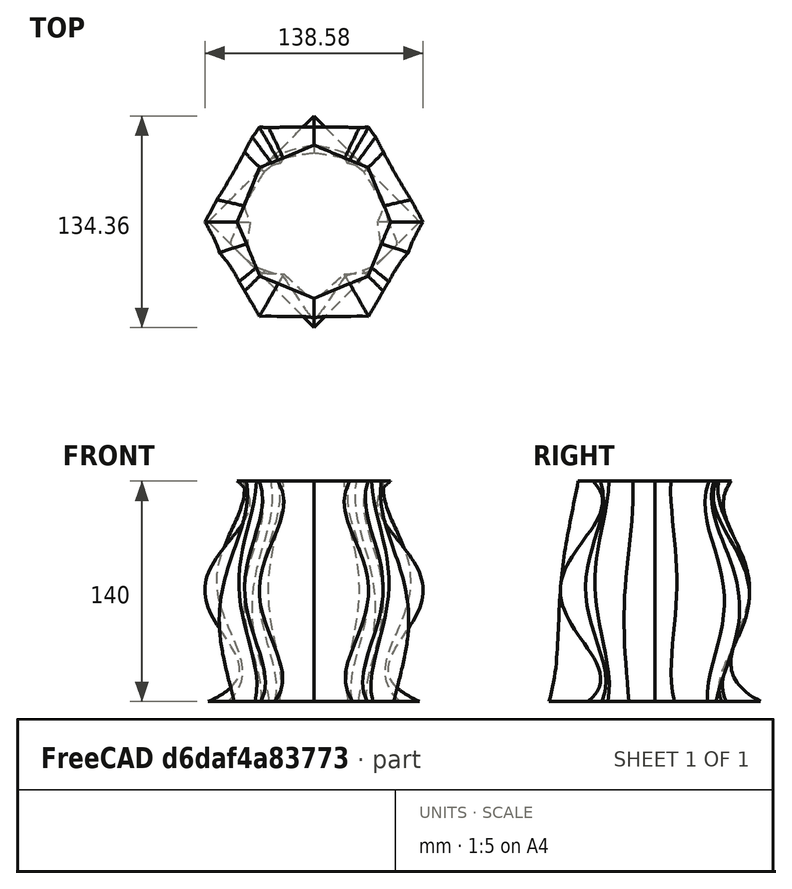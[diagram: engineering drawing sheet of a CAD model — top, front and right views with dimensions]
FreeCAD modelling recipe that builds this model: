
FCSTD DOCUMENT  (FreeCAD 0.18R16146 (Git))
Label: mama_vase
License: All rights reserved
LicenseURL: http://en.wikipedia.org/wiki/All_rights_reserved
objects: Sketcher::SketchObject×5, PartDesign::AdditiveLoft×1, PartDesign::Body×1
note: 8 computed .brp shape members not serialized (recipe doc carries the construction recipe); baked Part::Feature solids carry a one-line shape summary decoded from their .brp

FEATURE [Sketcher::SketchObject] Sketch001  label="4"
  MapMode = 5
  Support = -> [XY_Plane]
  sketch-geometry (4):
    g0: LineSegment StartX=0 StartY=67.1751 StartZ=0 EndX=67.1751 EndY=1.42e-14 EndZ=0
    g1: LineSegment StartX=67.1751 StartY=1.42e-14 StartZ=0 EndX=0 EndY=-67.1751 EndZ=0
    g2: LineSegment StartX=0 StartY=-67.1751 StartZ=0 EndX=-67.1751 EndY=2.84e-14 EndZ=0
    g3: LineSegment StartX=-67.1751 StartY=2.85e-14 StartZ=0 EndX=0 EndY=67.1751 EndZ=0
  constraints (11):
    c: Coincident(g0,g1)
    c: Coincident(g1,g2)
    c: Coincident(g2,g3)
    c: Coincident(g3,g0)
    c: Equal(g3,g0)
    c: Angle(g1,g2) = 1.5708
    c: Angle(g3,g0) = 1.5708
    c: Angle(g2,g3) = 1.5708
    c: Distance(g2) = 95  '4d'
    c: Symmetric(g0,g1,g-1)
    c: PointOnObject(g0,g-2)
FEATURE [Sketcher::SketchObject] Sketch003  label="5"
  AttachmentOffset = pos=(0,0,35) rot=(0,0,1;0rad)
  MapMode = 5
  Placement = pos=(0,0,35) rot=(0,0,1;0rad)
  Support = -> [XY_Plane]
  sketch-geometry (6):
    g0: LineSegment StartX=1.92e-14 StartY=-61.8034 StartZ=0 EndX=58.7785 EndY=-19.0983 EndZ=0
    g1: LineSegment StartX=58.7785 StartY=-19.0983 StartZ=0 EndX=36.3271 EndY=50 EndZ=0
    g2: LineSegment StartX=36.3271 StartY=50 StartZ=0 EndX=-36.3271 EndY=50 EndZ=0
    g3: LineSegment StartX=-36.3271 StartY=50 StartZ=0 EndX=-58.7785 EndY=-19.0983 EndZ=0
    g4: LineSegment StartX=-58.7785 StartY=-19.0983 StartZ=0 EndX=2.13e-14 EndY=-61.8034 EndZ=0
    g5: Circle [constr] CenterX=0 CenterY=0 CenterZ=0 NormalX=0 NormalY=0 NormalZ=1 AngleXU=0 Radius=50
  constraints (14):
    c: Coincident(g0,g1)
    c: Coincident(g1,g2)
    c: Coincident(g2,g3)
    c: Coincident(g3,g4)
    c: Coincident(g4,g0)
    c: Equal(g0, g1-g4) x4
    c: Tangent(g5,g1)
    c: Tangent(g5,g2)
    c: Tangent(g5,g3)
    c: Tangent(g5,g4)
    c: Tangent(g5,g0)
    c: Radius(g5) = 50  '5r'
    c: Coincident(g5,g-1)
    c: Horizontal(g2)
FEATURE [Sketcher::SketchObject] Sketch004  label="6"
  AttachmentOffset = pos=(0,0,70) rot=(0,0,1;0rad)
  MapMode = 5
  Placement = pos=(0,0,70) rot=(0,0,1;0rad)
  Support = -> [XY_Plane]
  sketch-geometry (7):
    g0: LineSegment StartX=69.282 StartY=0 StartZ=0 EndX=34.641 EndY=60 EndZ=0
    g1: LineSegment StartX=34.641 StartY=60 StartZ=0 EndX=-34.641 EndY=60 EndZ=0
    g2: LineSegment StartX=-34.641 StartY=60 StartZ=0 EndX=-69.282 EndY=-1.42e-14 EndZ=0
    g3: LineSegment StartX=-69.282 StartY=-1.42e-14 StartZ=0 EndX=-34.641 EndY=-60 EndZ=0
    g4: LineSegment StartX=-34.641 StartY=-60 StartZ=0 EndX=34.641 EndY=-60 EndZ=0
    g5: LineSegment StartX=34.641 StartY=-60 StartZ=0 EndX=69.282 EndY=0 EndZ=0
    g6: Circle [constr] CenterX=0 CenterY=0 CenterZ=0 NormalX=0 NormalY=0 NormalZ=1 AngleXU=0 Radius=69.282
  constraints (16):
    c: Coincident(g0,g1)
    c: Coincident(g1,g2)
    c: Coincident(g2,g3)
    c: Coincident(g3,g4)
    c: Coincident(g4,g5)
    c: Coincident(g5,g0)
    c: Equal(g0, g1-g5) x5
    c: PointOnObject(g0,g6)
    c: PointOnObject(g1,g6)
    c: PointOnObject(g2,g6)
    c: PointOnObject(g3,g6)
    c: PointOnObject(g4,g6)
    c: PointOnObject(g5,g6)
    c: PointOnObject(g5,g-1)
    c: Distance(g6,g0) = 60  '6r'
    c: Coincident(g6,g-1)
FEATURE [Sketcher::SketchObject] Sketch005  label="7"
  AttachmentOffset = pos=(0,0,105) rot=(0,0,1;0rad)
  MapMode = 5
  Placement = pos=(0,0,105) rot=(0,0,1;0rad)
  Support = -> [XY_Plane]
  sketch-geometry (8):
    g0: LineSegment StartX=7.1e-15 StartY=-55.4958 StartZ=0 EndX=43.3884 EndY=-34.6011 EndZ=0
    g1: LineSegment StartX=43.3884 StartY=-34.6011 StartZ=0 EndX=54.1044 EndY=12.349 EndZ=0
    g2: LineSegment StartX=54.1044 StartY=12.349 StartZ=0 EndX=24.0787 EndY=50 EndZ=0
    g3: LineSegment StartX=24.0787 StartY=50 StartZ=0 EndX=-24.0787 EndY=50 EndZ=0
    g4: LineSegment StartX=-24.0787 StartY=50 StartZ=0 EndX=-54.1044 EndY=12.349 EndZ=0
    g5: LineSegment StartX=-54.1044 StartY=12.349 StartZ=0 EndX=-43.3884 EndY=-34.6011 EndZ=0
    g6: LineSegment StartX=-43.3884 StartY=-34.6011 StartZ=0 EndX=7.1e-15 EndY=-55.4958 EndZ=0
    g7: Circle [constr] CenterX=0 CenterY=0 CenterZ=0 NormalX=0 NormalY=0 NormalZ=1 AngleXU=0 Radius=55.4958
  constraints (18):
    c: Coincident(g0,g1)
    c: Coincident(g1,g2)
    c: Coincident(g2,g3)
    c: Coincident(g3,g4)
    c: Coincident(g4,g5)
    c: Coincident(g5,g6)
    c: Coincident(g6,g0)
    c: Equal(g0, g1-g6) x6
    c: PointOnObject(g0,g7)
    c: PointOnObject(g1,g7)
    c: PointOnObject(g2,g7)
    c: PointOnObject(g3,g7)
    c: PointOnObject(g4,g7)
    c: PointOnObject(g5,g7)
    c: PointOnObject(g6,g7)
    c: Distance(g7,g1) = 50  '7r'
    c: Coincident(g7,g-1)
    c: Horizontal(g3)
FEATURE [Sketcher::SketchObject] Sketch006  label="8"
  AttachmentOffset = pos=(0,0,140) rot=(0,0,1;0rad)
  MapMode = 5
  Placement = pos=(0,0,140) rot=(0,0,1;0rad)
  Support = -> [XY_Plane]
  sketch-geometry (9):
    g0: LineSegment StartX=-2.5e-15 StartY=-48.7076 StartZ=0 EndX=34.4415 EndY=-34.4415 EndZ=0
    g1: LineSegment StartX=34.4415 StartY=-34.4415 StartZ=0 EndX=48.7076 EndY=-7.1e-15 EndZ=0
    g2: LineSegment StartX=48.7076 StartY=-4.3e-15 StartZ=0 EndX=34.4415 EndY=34.4415 EndZ=0
    g3: LineSegment StartX=34.4415 StartY=34.4415 StartZ=0 EndX=0 EndY=48.7076 EndZ=0
    g4: LineSegment StartX=0 StartY=48.7076 StartZ=0 EndX=-34.4415 EndY=34.4415 EndZ=0
    g5: LineSegment StartX=-34.4415 StartY=34.4415 StartZ=0 EndX=-48.7076 EndY=0 EndZ=0
    g6: LineSegment StartX=-48.7076 StartY=-9e-16 StartZ=0 EndX=-34.4415 EndY=-34.4415 EndZ=0
    g7: LineSegment StartX=-34.4415 StartY=-34.4415 StartZ=0 EndX=0 EndY=-48.7076 EndZ=0
    g8: Circle [constr] CenterX=0 CenterY=0 CenterZ=0 NormalX=0 NormalY=0 NormalZ=1 AngleXU=0 Radius=48.7076
  constraints (20):
    c: Coincident(g0,g1)
    c: Coincident(g1,g2)
    c: Coincident(g2,g3)
    c: Coincident(g3,g4)
    c: Coincident(g4,g5)
    c: Coincident(g5,g6)
    c: Coincident(g6,g7)
    c: Coincident(g7,g0)
    c: Equal(g0, g1-g7) x7
    c: PointOnObject(g0,g8)
    c: PointOnObject(g1,g8)
    c: PointOnObject(g2,g8)
    c: PointOnObject(g3,g8)
    c: PointOnObject(g4,g8)
    c: PointOnObject(g5,g8)
    c: PointOnObject(g6,g8)
    c: PointOnObject(g7,g8)
    c: Distance(g8,g1) = 45  '8r'
    c: Coincident(g8,g-1)
    c: PointOnObject(g3,g-2)
FEATURE [PartDesign::AdditiveLoft] AdditiveLoft
  Closed = false
  Profile = -> Sketch001
  Refine = true
  Ruled = false
  Sections = -> [Sketch003,Sketch004,Sketch005,Sketch006]
FEATURE [PartDesign::Body] Body
  Group = -> [Sketch001,Sketch003,Sketch004,Sketch005,Sketch006,AdditiveLoft]
  Origin = -> Origin
  Tip = -> AdditiveLoft
